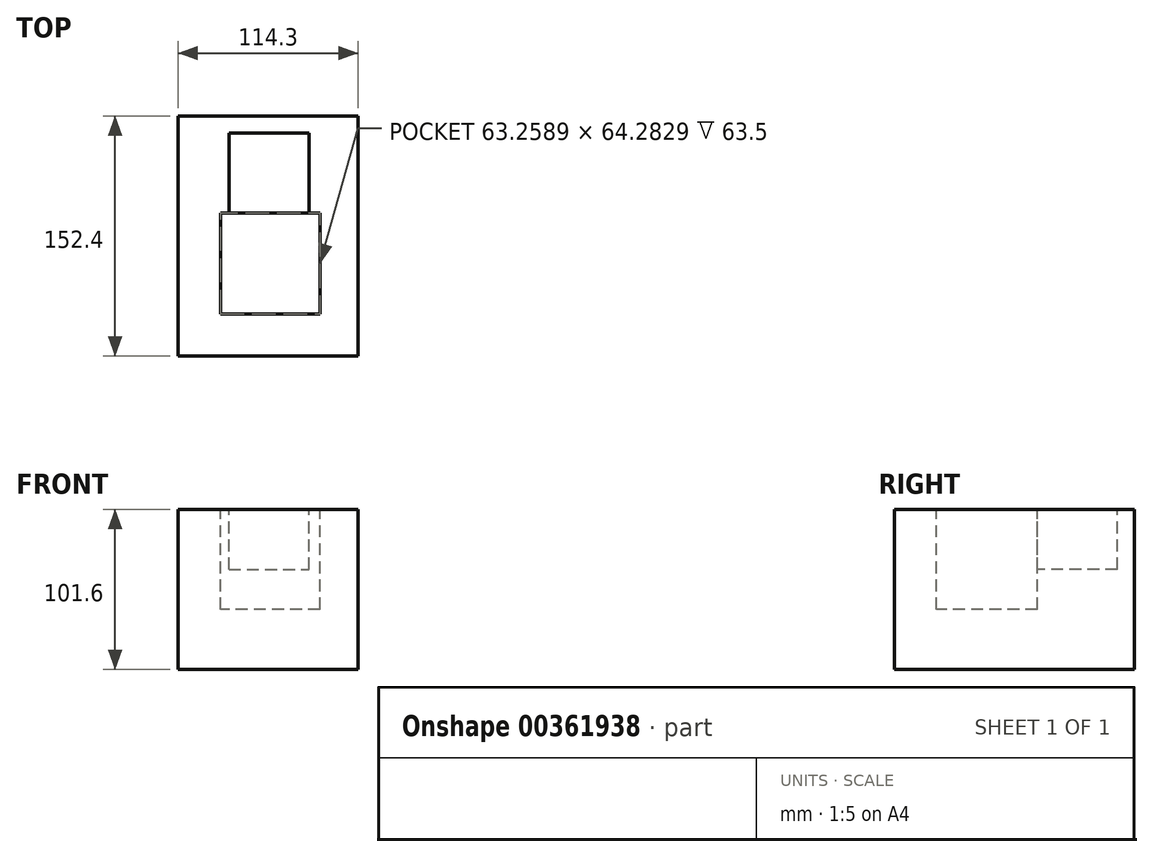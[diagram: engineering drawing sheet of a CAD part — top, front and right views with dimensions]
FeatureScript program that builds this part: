
annotation { "Feature Type Name" : "Feature", "Feature Type Description" : "" }
export const myFeature = defineFeature(function(context is Context, id is Id, definition is map)
    precondition{}
    {
        {
            var Q0;
            Q0=qCreatedBy(makeId("Top.planeOp"),FACE);
            var sketch = newSketch(context, id + "F0", { "sketchPlane" : qUnion([Q0])});
            skLineSegment(sketch, "E0", {"start": v(-63.87, 102.72) * mm, "end": v(50.43, 102.72) * mm});
            skLineSegment(sketch, "E1", {"start": v(-63.87, 102.72) * mm, "end": v(-63.87, -49.68) * mm});
            skLineSegment(sketch, "E2", {"start": v(-63.87, -49.68) * mm, "end": v(50.43, -49.68) * mm});
            skLineSegment(sketch, "E3", {"start": v(50.43, -49.68) * mm, "end": v(50.43, 102.72) * mm});
            skSolve(sketch);
        }
        {
            var Q0;
            Q0=makeQuery(id+"F0.imprint","IMPRINT",FACE,{"disambiguationData":[TD([[makeQuery(id+"F0.imprint","IMPRINT",EDGE,{"derivedFrom":sQuery(id+"F0.wireOp",EDGE,"E0")}),-1.0]])]});
            extrude(context, id + "F1", {"entities" : qUnion([Q0]), "depth" : 101.6 * mm});
        }
        {
            var Q0;
            Q0=makeQuery(id+"F1.opExtrude","CAP_FACE",FACE,{"disambiguationData":[OSD([sQuery(id+"F0.wireOp",EDGE,"E0"),sQuery(id+"F0.wireOp",EDGE,"E1"),sQuery(id+"F0.wireOp",EDGE,"E2"),sQuery(id+"F0.wireOp",EDGE,"E3")])],"isStart":false});
            var sketch = newSketch(context, id + "F2", { "sketchPlane" : qUnion([Q0])});
            skLineSegment(sketch, "E4", {"start": v(-31.58, 92.03) * mm, "end": v(19.22, 92.03) * mm});
            skLineSegment(sketch, "E5", {"start": v(-31.58, 92.03) * mm, "end": v(-31.58, 41.23) * mm});
            skLineSegment(sketch, "E6", {"start": v(19.22, 92.03) * mm, "end": v(19.22, 41.23) * mm});
            skLineSegment(sketch, "E7", {"start": v(19.22, 41.23) * mm, "end": v(-31.58, 41.23) * mm});
            skSolve(sketch);
        }
        {
            var Q0;
            Q0=makeQuery(id+"F2.imprint","IMPRINT",FACE,{"disambiguationData":[TD([[makeQuery(id+"F2.imprint","IMPRINT",EDGE,{"derivedFrom":sQuery(id+"F2.wireOp",EDGE,"E4")}),-1.0]])]});
            extrude(context, id + "F3", {"entities" : qUnion([Q0]), "operationType" : NewBodyOperationType.REMOVE, "oppositeDirection" : true, "depth" : 38.1 * mm});
        }
        {
            var Q0;
            Q0=makeQuery(id+"F1.opExtrude","CAP_FACE",FACE,{"disambiguationData":[OSD([sQuery(id+"F0.wireOp",EDGE,"E0"),sQuery(id+"F0.wireOp",EDGE,"E1"),sQuery(id+"F0.wireOp",EDGE,"E2"),sQuery(id+"F0.wireOp",EDGE,"E3")])],"isStart":false});
            var sketch = newSketch(context, id + "F4", { "sketchPlane" : qUnion([Q0])});
            skLineSegment(sketch, "E8", {"start": v(-31.58, 41.23) * mm, "end": v(-36.93, 41.23) * mm});
            skLineSegment(sketch, "E9", {"start": v(-36.93, 41.23) * mm, "end": v(-36.93, -23.05) * mm});
            skLineSegment(sketch, "E10", {"start": v(-36.93, -23.05) * mm, "end": v(26.32, -23.05) * mm});
            skLineSegment(sketch, "E11", {"start": v(26.32, -23.05) * mm, "end": v(26.32, 41.23) * mm});
            skLineSegment(sketch, "E12", {"start": v(26.32, 41.23) * mm, "end": v(19.22, 41.23) * mm});
            skLineSegment(sketch, "E13", {"start": v(19.22, 41.23) * mm, "end": v(-31.58, 41.23) * mm});
            skSolve(sketch);
        }
        {
            var Q0;
            Q0=makeQuery(id+"F4.imprint","IMPRINT",FACE,{"disambiguationData":[TD([[makeQuery(id+"F4.imprint","IMPRINT",EDGE,{"derivedFrom":sQuery(id+"F4.wireOp",EDGE,"E8")}),1.0]])]});
            extrude(context, id + "F5", {"entities" : qUnion([Q0]), "operationType" : NewBodyOperationType.REMOVE, "oppositeDirection" : true, "depth" : 63.5 * mm});
        }
    });
